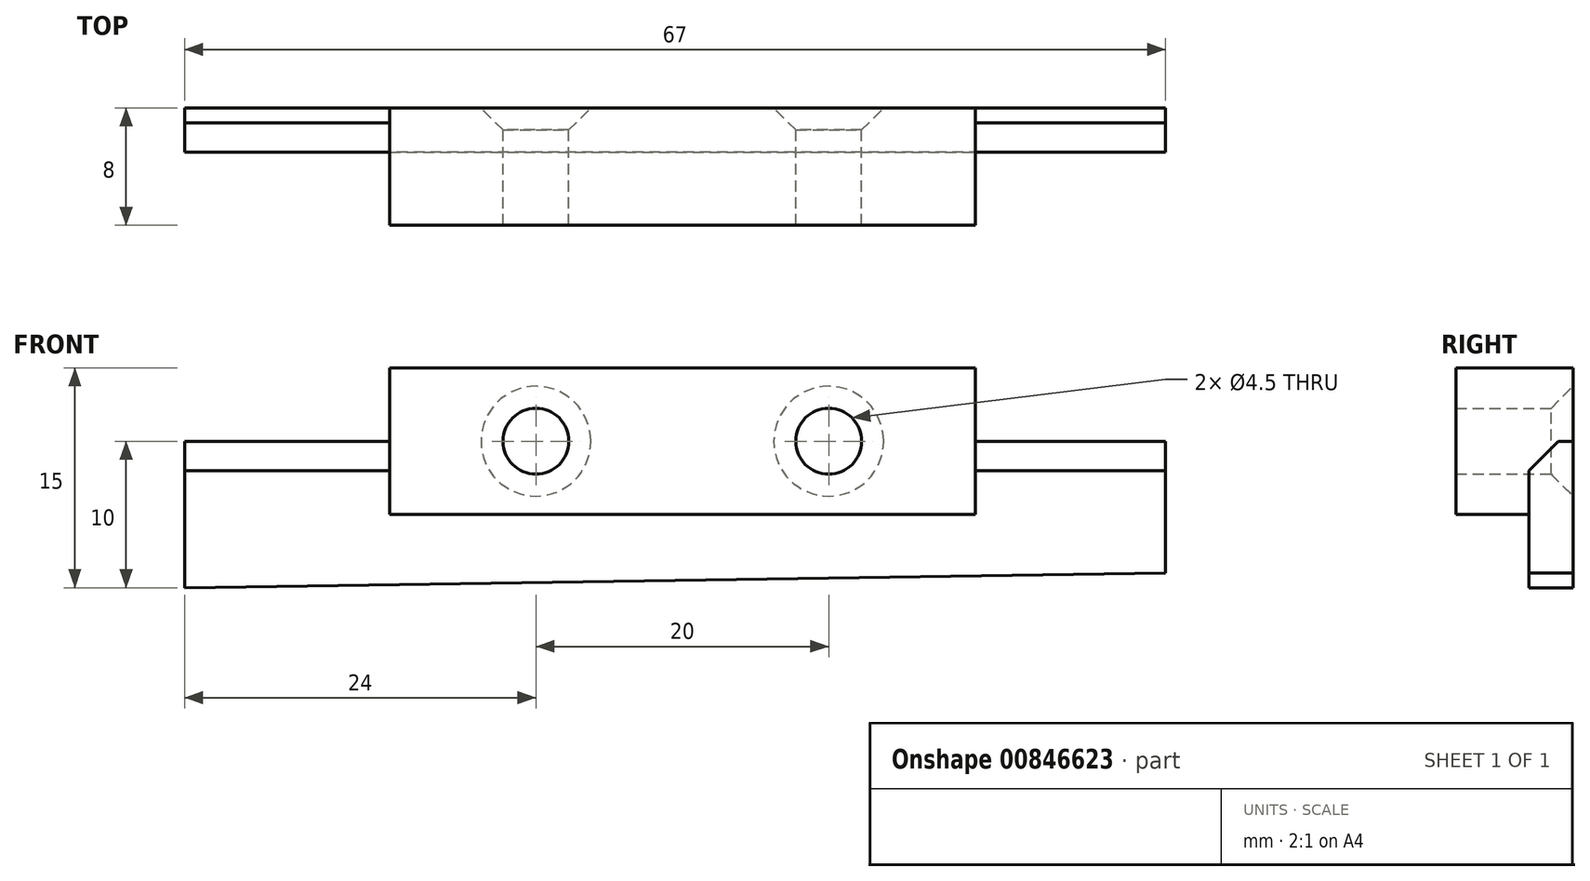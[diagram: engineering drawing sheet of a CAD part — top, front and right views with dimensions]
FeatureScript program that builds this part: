
annotation { "Feature Type Name" : "Feature", "Feature Type Description" : "" }
export const myFeature = defineFeature(function(context is Context, id is Id, definition is map)
    precondition{}
    {
        {
            var Q0;
            Q0=qCreatedBy(makeId("Front.planeOp"),FACE);
            var sketch = newSketch(context, id + "F0", { "sketchPlane" : qUnion([Q0])});
            skLineSegment(sketch, "E0.bottom", {"start": v(-20, 5) * mm, "end": v(20, 5) * mm});
            skLineSegment(sketch, "E0.top", {"start": v(-20, -5) * mm, "end": v(20, -5) * mm});
            skLineSegment(sketch, "E0.left", {"start": v(-20, 5) * mm, "end": v(-20, -5) * mm});
            skLineSegment(sketch, "E0.right", {"start": v(20, 5) * mm, "end": v(20, -5) * mm});
            skPoint(sketch, "E0.middle", {"position": v(0, 0) * mm});
            skLineSegment(sketch, "E1", {"start": v(0, 0) * mm, "end": v(33, 0) * mm, "construction": true});
            skPoint(sketch, "E1.endSnap0", {"position": v(20, 0) * mm});
            skLineSegment(sketch, "E2", {"start": v(33, 0) * mm, "end": v(33, -9) * mm});
            skLineSegment(sketch, "E3", {"start": v(0, 0) * mm, "end": v(-34, 0) * mm, "construction": true});
            skLineSegment(sketch, "E4", {"start": v(-34, 0) * mm, "end": v(-34, -10) * mm});
            skLineSegment(sketch, "E5", {"start": v(33, -9) * mm, "end": v(-34, -10) * mm});
            skLineSegment(sketch, "E6", {"start": v(20, 0) * mm, "end": v(33, 0) * mm});
            skLineSegment(sketch, "E7", {"start": v(-34, 0) * mm, "end": v(-20, 0) * mm});
            skPoint(sketch, "E8", {"position": v(10, 0) * mm});
            skPoint(sketch, "E9", {"position": v(-10, 0) * mm});
            skCircle(sketch, "E10", {"center": v(-10, 0) * mm, "radius": 2.25 * mm});
            skCircle(sketch, "E11", {"center": v(10, 0) * mm, "radius": 2.25 * mm});
            skSolve(sketch);
        }
        {
            var Q0;
            {var subQ1=sQuery(id+"F0.wireOp",EDGE,"E0.top");Q0=makeQuery(id+"F0.imprint","IMPRINT",FACE,{"disambiguationData":[TD([[makeQuery(id+"F0.imprint","IMPRINT",EDGE,{"derivedFrom":subQ1}),-1.0]])]});}
            extrude(context, id + "F1", {"entities" : qUnion([Q0]), "depth" : 3 * mm, "offsetDistance" : 25 * mm});
        }
        {
            var Q0;
            {var subQ3=sQuery(id+"F0.wireOp",EDGE,"E0.bottom");Q0=makeQuery(id+"F0.imprint","IMPRINT",FACE,{"disambiguationData":[TD([[makeQuery(id+"F0.imprint","IMPRINT",EDGE,{"derivedFrom":subQ3}),-1.0]])]});}
            extrude(context, id + "F2", {"entities" : qUnion([Q0]), "operationType" : NewBodyOperationType.ADD, "depth" : 8 * mm, "offsetDistance" : 25 * mm});
        }
        {
            var Q0;
            Q0=makeQuery(id+"F2.opExtrude","CAP_EDGE",EDGE,{"disambiguationData":[OSD([sQuery(id+"F0.wireOp",EDGE,"E11")])],"isStart":true});
            var Q1;
            Q1=makeQuery(id+"F2.opExtrude","CAP_EDGE",EDGE,{"disambiguationData":[OSD([sQuery(id+"F0.wireOp",EDGE,"E10")])],"isStart":true});
            chamfer(context, id + "F3", {"entities" : qUnion([Q0, Q1]), "width" : 1.5 * mm, "tangentPropagation" : true});
        }
        {
            var Q0;
            Q0=makeQuery(id+"F1.opExtrude","CAP_EDGE",EDGE,{"disambiguationData":[OSD([sQuery(id+"F0.wireOp",EDGE,"E7")])],"isStart":false});
            var Q1;
            Q1=makeQuery(id+"F1.opExtrude","CAP_EDGE",EDGE,{"disambiguationData":[OSD([sQuery(id+"F0.wireOp",EDGE,"E6")])],"isStart":false});
            chamfer(context, id + "F4", {"entities" : qUnion([Q0, Q1]), "width" : 2 * mm, "tangentPropagation" : true});
        }
    });
